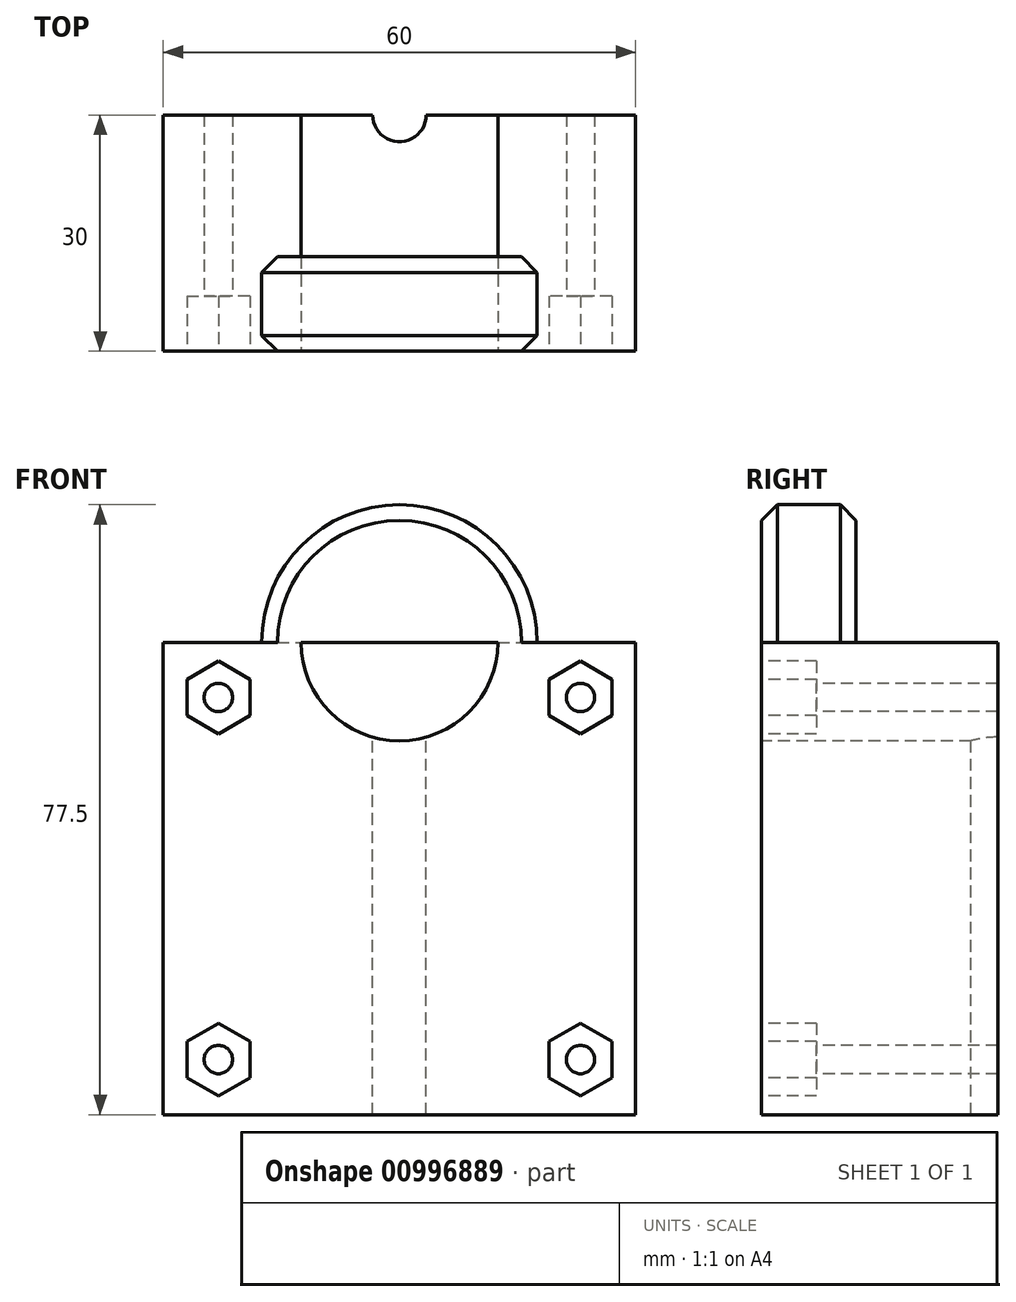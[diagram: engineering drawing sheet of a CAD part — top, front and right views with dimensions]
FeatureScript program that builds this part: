
annotation { "Feature Type Name" : "Feature", "Feature Type Description" : "" }
export const myFeature = defineFeature(function(context is Context, id is Id, definition is map)
    precondition{}
    {
        {
            var Q0;
            Q0=qCreatedBy(makeId("Top.planeOp"),FACE);
            var sketch = newSketch(context, id + "F0", { "sketchPlane" : qUnion([Q0])});
            skLineSegment(sketch, "E0.bottom", {"start": v(30, -15) * mm, "end": v(-30, -15) * mm});
            skLineSegment(sketch, "E0.top", {"start": v(30, 15) * mm, "end": v(-30, 15) * mm});
            skLineSegment(sketch, "E0.left", {"start": v(30, -15) * mm, "end": v(30, 15) * mm});
            skLineSegment(sketch, "E0.right", {"start": v(-30, -15) * mm, "end": v(-30, 15) * mm});
            skPoint(sketch, "E0.middle", {"position": v(0, 0) * mm});
            skSolve(sketch);
        }
        {
            var Q0;
            Q0=qSketchRegion(id+"F0",true);
            extrude(context, id + "F1", {"entities" : qUnion([Q0]), "depth" : 60 * mm, "offsetDistance" : 25 * mm});
        }
        {
            var Q0;
            Q0=makeQuery(id+"F1.opExtrude","CAP_FACE",FACE,{"disambiguationData":[OSD([sQuery(id+"F0.wireOp",EDGE,"E0.bottom"),sQuery(id+"F0.wireOp",EDGE,"E0.top"),sQuery(id+"F0.wireOp",EDGE,"E0.left"),sQuery(id+"F0.wireOp",EDGE,"E0.right")])],"isStart":false});
            var sketch = newSketch(context, id + "F2", { "sketchPlane" : qUnion([Q0])});
            skPoint(sketch, "E1", {"position": v(0, 15) * mm});
            skCircle(sketch, "E2", {"center": v(0, 15) * mm, "radius": 3.4 * mm});
            skSolve(sketch);
        }
        {
            var Q0;
            Q0=qSketchRegion(id+"F2",true);
            extrude(context, id + "F3", {"entities" : qUnion([Q0]), "operationType" : NewBodyOperationType.REMOVE, "endBound" : BoundingType.THROUGH_ALL, "oppositeDirection" : true, "depth" : 25 * mm, "offsetDistance" : 25 * mm});
        }
        {
            var Q0;
            Q0=makeQuery(id+"F1.opExtrude","SWEPT_FACE",FACE,{"disambiguationData":[OSD([sQuery(id+"F0.wireOp",EDGE,"E0.bottom")])]});
            var sketch = newSketch(context, id + "F4", { "sketchPlane" : qUnion([Q0])});
            skPoint(sketch, "E3", {"position": v(-23, 53) * mm});
            skPoint(sketch, "E4", {"position": v(23, 53) * mm});
            skPoint(sketch, "E5", {"position": v(23, 7) * mm});
            skPoint(sketch, "E6", {"position": v(-23, 7) * mm});
            skCircle(sketch, "E7", {"center": v(-23, 53) * mm, "radius": 1.8 * mm});
            skCircle(sketch, "E8", {"center": v(23, 53) * mm, "radius": 1.8 * mm});
            skCircle(sketch, "E9", {"center": v(23, 7) * mm, "radius": 1.8 * mm});
            skCircle(sketch, "E10", {"center": v(-23, 7) * mm, "radius": 1.8 * mm});
            skSolve(sketch);
        }
        {
            var Q0;
            Q0=qSketchRegion(id+"F4",true);
            extrude(context, id + "F5", {"entities" : qUnion([Q0]), "operationType" : NewBodyOperationType.REMOVE, "endBound" : BoundingType.THROUGH_ALL, "oppositeDirection" : true, "depth" : 25 * mm, "offsetDistance" : 25 * mm});
        }
        {
            var Q0;
            Q0=makeQuery(id+"F1.opExtrude","SWEPT_FACE",FACE,{"disambiguationData":[OSD([sQuery(id+"F0.wireOp",EDGE,"E0.bottom")])]});
            var sketch = newSketch(context, id + "F6", { "sketchPlane" : qUnion([Q0])});
            skPoint(sketch, "E11", {"position": v(-23, 53) * mm});
            skCircle(sketch, "E12.cCircle", {"center": v(-23, 53) * mm, "radius": 4.62 * mm, "construction": true});
            skLineSegment(sketch, "E12.0", {"start": v(-19, 50.7) * mm, "end": v(-23, 48.38) * mm});
            skLineSegment(sketch, "E12.1", {"start": v(-23, 48.38) * mm, "end": v(-27, 50.7) * mm});
            skLineSegment(sketch, "E12.2", {"start": v(-27, 50.7) * mm, "end": v(-27, 55.3) * mm});
            skLineSegment(sketch, "E12.3", {"start": v(-27, 55.3) * mm, "end": v(-23, 57.62) * mm});
            skLineSegment(sketch, "E12.4", {"start": v(-23, 57.62) * mm, "end": v(-19, 55.3) * mm});
            skLineSegment(sketch, "E12.5", {"start": v(-19, 55.3) * mm, "end": v(-19, 50.7) * mm});
            skSolve(sketch);
        }
        {
            var Q0;
            Q0 = qSketchRegion(id + "F6", true);
            extrude(context, id + "F7", {"entities" : qUnion([Q0]), "operationType" : NewBodyOperationType.REMOVE, "oppositeDirection" : true, "depth" : 7 * mm, "offsetDistance" : 25 * mm});
        }
        {
            var Q0;
            Q0=makeQuery(id+"F1.opExtrude","SWEPT_FACE",FACE,{"disambiguationData":[OSD([sQuery(id+"F0.wireOp",EDGE,"E0.bottom")])]});
            var sketch = newSketch(context, id + "F8", { "sketchPlane" : qUnion([Q0])});
            skPoint(sketch, "E13", {"position": v(23, 53) * mm});
            skCircle(sketch, "E14.cCircle", {"center": v(23, 53) * mm, "radius": 4.62 * mm, "construction": true});
            skLineSegment(sketch, "E14.0", {"start": v(23, 48.38) * mm, "end": v(19, 50.7) * mm});
            skLineSegment(sketch, "E14.1", {"start": v(19, 50.7) * mm, "end": v(19, 55.3) * mm});
            skLineSegment(sketch, "E14.2", {"start": v(19, 55.3) * mm, "end": v(23, 57.62) * mm});
            skLineSegment(sketch, "E14.3", {"start": v(23, 57.62) * mm, "end": v(27, 55.3) * mm});
            skLineSegment(sketch, "E14.4", {"start": v(27, 55.3) * mm, "end": v(27, 50.7) * mm});
            skLineSegment(sketch, "E14.5", {"start": v(27, 50.7) * mm, "end": v(23, 48.38) * mm});
            skSolve(sketch);
        }
        {
            var Q0;
            Q0 = qSketchRegion(id + "F8", true);
            extrude(context, id + "F9", {"entities" : qUnion([Q0]), "operationType" : NewBodyOperationType.REMOVE, "oppositeDirection" : true, "depth" : 7 * mm, "offsetDistance" : 25 * mm});
        }
        {
            var Q0;
            Q0=makeQuery(id+"F1.opExtrude","SWEPT_FACE",FACE,{"disambiguationData":[OSD([sQuery(id+"F0.wireOp",EDGE,"E0.bottom")])]});
            var sketch = newSketch(context, id + "F10", { "sketchPlane" : qUnion([Q0])});
            skPoint(sketch, "E15", {"position": v(-23, 7) * mm});
            skCircle(sketch, "E16.cCircle", {"center": v(-23, 7) * mm, "radius": 4.62 * mm, "construction": true});
            skLineSegment(sketch, "E16.0", {"start": v(-19, 4.7) * mm, "end": v(-23, 2.38) * mm});
            skLineSegment(sketch, "E16.1", {"start": v(-23, 2.38) * mm, "end": v(-27, 4.7) * mm});
            skLineSegment(sketch, "E16.2", {"start": v(-27, 4.7) * mm, "end": v(-27, 9.3) * mm});
            skLineSegment(sketch, "E16.3", {"start": v(-27, 9.3) * mm, "end": v(-23, 11.62) * mm});
            skLineSegment(sketch, "E16.4", {"start": v(-23, 11.62) * mm, "end": v(-19, 9.3) * mm});
            skLineSegment(sketch, "E16.5", {"start": v(-19, 9.3) * mm, "end": v(-19, 4.7) * mm});
            skSolve(sketch);
        }
        {
            var Q0;
            Q0 = qSketchRegion(id + "F10", true);
            extrude(context, id + "F11", {"entities" : qUnion([Q0]), "operationType" : NewBodyOperationType.REMOVE, "oppositeDirection" : true, "depth" : 7 * mm, "offsetDistance" : 25 * mm});
        }
        {
            var Q0;
            Q0=makeQuery(id+"F1.opExtrude","SWEPT_FACE",FACE,{"disambiguationData":[OSD([sQuery(id+"F0.wireOp",EDGE,"E0.bottom")])]});
            var sketch = newSketch(context, id + "F12", { "sketchPlane" : qUnion([Q0])});
            skPoint(sketch, "E17", {"position": v(23, 7) * mm});
            skCircle(sketch, "E18.cCircle", {"center": v(23, 7) * mm, "radius": 4.62 * mm, "construction": true});
            skLineSegment(sketch, "E18.0", {"start": v(27, 4.7) * mm, "end": v(23, 2.38) * mm});
            skLineSegment(sketch, "E18.1", {"start": v(23, 2.38) * mm, "end": v(19, 4.7) * mm});
            skLineSegment(sketch, "E18.2", {"start": v(19, 4.7) * mm, "end": v(19, 9.3) * mm});
            skLineSegment(sketch, "E18.3", {"start": v(19, 9.3) * mm, "end": v(23, 11.62) * mm});
            skLineSegment(sketch, "E18.4", {"start": v(23, 11.62) * mm, "end": v(27, 9.3) * mm});
            skLineSegment(sketch, "E18.5", {"start": v(27, 9.3) * mm, "end": v(27, 4.7) * mm});
            skSolve(sketch);
        }
        {
            var Q0;
            Q0 = qSketchRegion(id + "F12", true);
            extrude(context, id + "F13", {"entities" : qUnion([Q0]), "operationType" : NewBodyOperationType.REMOVE, "oppositeDirection" : true, "depth" : 7 * mm, "offsetDistance" : 25 * mm});
        }
        {
            var Q0;
            Q0=makeQuery(id+"F1.opExtrude","SWEPT_FACE",FACE,{"disambiguationData":[OSD([sQuery(id+"F0.wireOp",EDGE,"E0.bottom")])]});
            var sketch = newSketch(context, id + "F14", { "sketchPlane" : qUnion([Q0])});
            skPoint(sketch, "E19", {"position": v(0, 60) * mm});
            skCircle(sketch, "E20", {"center": v(0, 60) * mm, "radius": 17.5 * mm});
            skSolve(sketch);
        }
        {
            var Q0;
            Q0 = qSketchRegion(id + "F14", true);
            extrude(context, id + "F15", {"entities" : qUnion([Q0]), "operationType" : NewBodyOperationType.ADD, "oppositeDirection" : true, "depth" : 12 * mm, "offsetDistance" : 25 * mm});
        }
        {
            var Q0;
            Q0=makeQuery(id+"F15.boolean.opBoolean","MERGE",FACE,{"derivedFrom":[makeQuery(id+"F1.opExtrude","SWEPT_FACE",FACE,{"disambiguationData":[OSD([sQuery(id+"F0.wireOp",EDGE,"E0.bottom")])]}),makeQuery(id+"F15.opExtrude","CAP_FACE",FACE,{"disambiguationData":[OSD([sQuery(id+"F14.wireOp",EDGE,"E20")])],"isStart":true})]});
            var sketch = newSketch(context, id + "F16", { "sketchPlane" : qUnion([Q0])});
            skLineSegment(sketch, "E21", {"start": v(0, 77.5) * mm, "end": v(0, 0) * mm, "construction": true});
            skPoint(sketch, "E22", {"position": v(0, 60) * mm});
            skCircle(sketch, "E23", {"center": v(0, 60) * mm, "radius": 12.5 * mm});
            skLineSegment(sketch, "E24", {"start": v(-30, 60) * mm, "end": v(30, 60) * mm});
            skSolve(sketch);
        }
        {
            var Q0;
            {var subQ0=sQuery(id+"F16.wireOp",EDGE,"E24");var subQ1=sQuery(id+"F16.wireOp",EDGE,"E23");var subQ2=makeQuery(id+"F16.imprint","INTERSECT",VERTEX,{"disambiguationData":[OD(0.0)],"derivedFrom":[subQ1,subQ0]});Q0=makeQuery(id+"F16.imprint","IMPRINT",FACE,{"disambiguationData":[TD([[makeQuery(id+"F16.imprint","IMPRINT",EDGE,{"disambiguationData":[TD([[subQ2,1.0]])],"derivedFrom":subQ1}),1.0]])]});}
            extrude(context, id + "F17", {"entities" : qUnion([Q0]), "operationType" : NewBodyOperationType.REMOVE, "endBound" : BoundingType.THROUGH_ALL, "oppositeDirection" : true, "depth" : 25 * mm, "offsetDistance" : 25 * mm});
        }
        {
            var Q0;
            Q0=makeQuery(id+"F15.opExtrude","CAP_EDGE",EDGE,{"disambiguationData":[OSD([sQuery(id+"F14.wireOp",EDGE,"E20")])],"isStart":true});
            var Q1;
            Q1=makeQuery(id+"F15.opExtrude","CAP_EDGE",EDGE,{"disambiguationData":[OSD([sQuery(id+"F14.wireOp",EDGE,"E20")])],"isStart":false});
            var Q2;
            Q2=makeQuery(id+"F17.boolean.opBoolean","COPY",EDGE,{"derivedFrom":makeQuery(id+"F17.opExtrude","CAP_EDGE",EDGE,{"disambiguationData":[OSD([sQuery(id+"F16.wireOp",EDGE,"E23")])],"isStart":true})});
            var Q3;
            Q3=makeQuery(id+"F17.boolean.opBoolean","INTERSECT",EDGE,{"derivedFrom":[makeQuery(id+"F15.opExtrude","CAP_FACE",FACE,{"disambiguationData":[OSD([sQuery(id+"F14.wireOp",EDGE,"E20")])],"isStart":false}),makeQuery(id+"F17.opExtrude","SWEPT_FACE",FACE,{"disambiguationData":[OSD([sQuery(id+"F16.wireOp",EDGE,"E23")])]})]});
            chamfer(context, id + "F18", {"entities" : qUnion([Q0, Q1, Q2, Q3]), "width" : 2 * mm, "tangentPropagation" : true});
        }
    });
